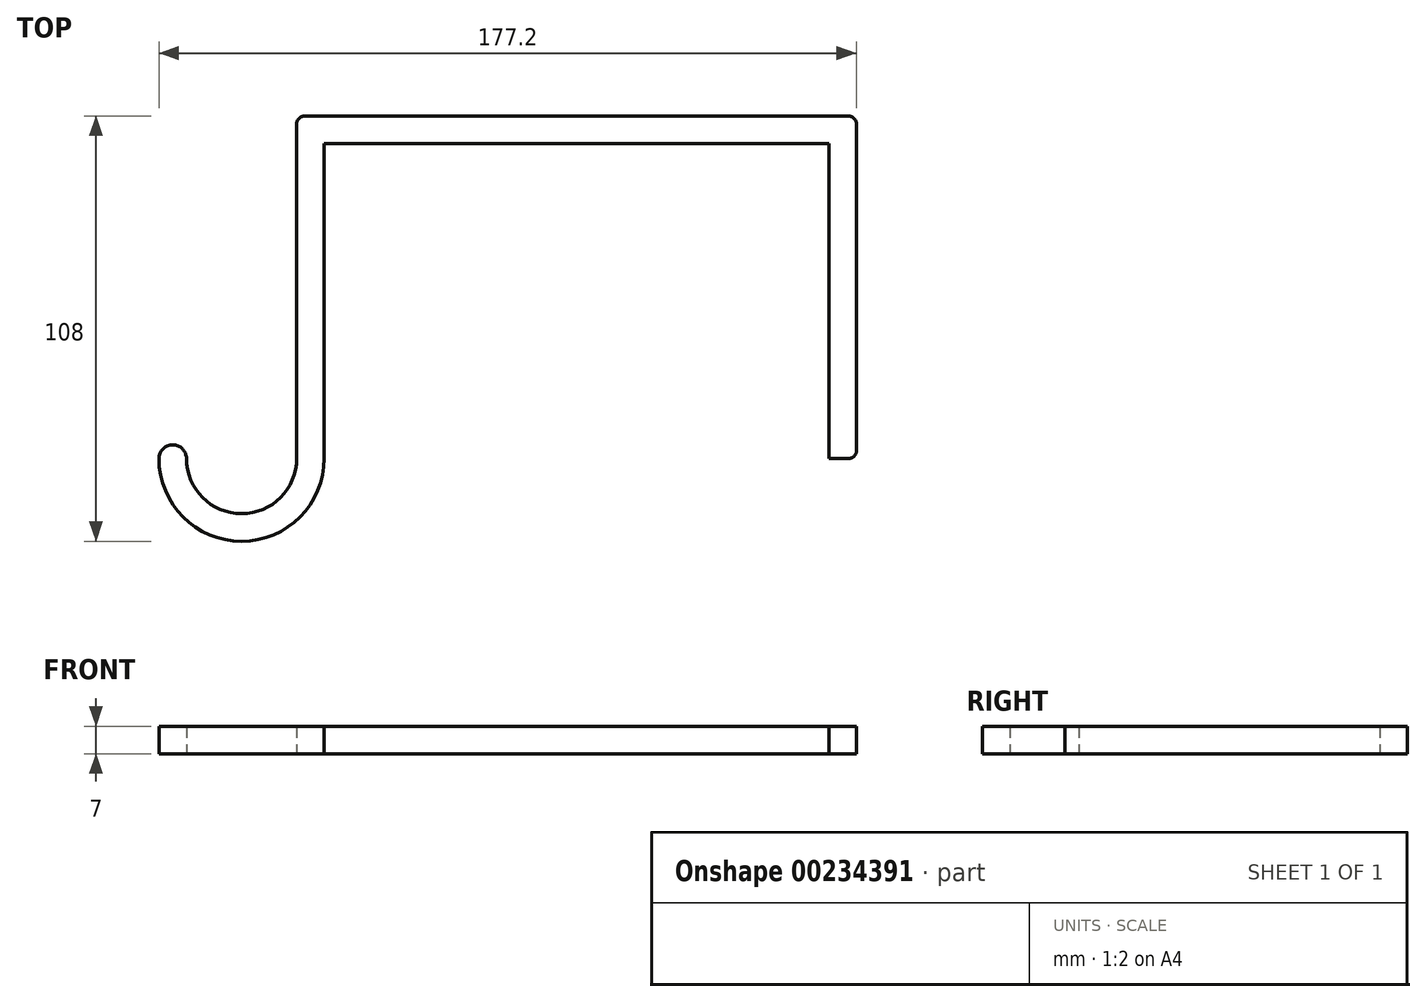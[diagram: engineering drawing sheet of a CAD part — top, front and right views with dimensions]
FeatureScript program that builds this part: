
annotation { "Feature Type Name" : "Feature", "Feature Type Description" : "" }
export const myFeature = defineFeature(function(context is Context, id is Id, definition is map)
    precondition{}
    {
        {
            assignVariable(context, id + "F0", {"name" : "D", "anyValue" : 7});
        }
        {
            var Q0;
            Q0=qCreatedBy(makeId("Top.planeOp"),FACE);
            var sketch = newSketch(context, id + "F1", { "sketchPlane" : qUnion([Q0])});
            skArc(sketch, "E0", {"start": v(-14, 0) * mm, "mid": v(0, -14) * mm, "end": v(14, 0) * mm});
            skLineSegment(sketch, "E1", {"start": v(14, 0) * mm, "end": v(14, 85) * mm});
            skLineSegment(sketch, "E2", {"start": v(16, 87) * mm, "end": v(154.2, 87) * mm});
            skLineSegment(sketch, "E3", {"start": v(156.2, 85) * mm, "end": v(156.2, 2) * mm});
            skLineSegment(sketch, "E4", {"start": v(154.2, 0) * mm, "end": v(149.2, 0) * mm});
            skLineSegment(sketch, "E5", {"start": v(149.2, 0) * mm, "end": v(149.2, 80) * mm});
            skLineSegment(sketch, "E6", {"start": v(149.2, 80) * mm, "end": v(21, 80) * mm});
            skLineSegment(sketch, "E7", {"start": v(21, 80) * mm, "end": v(21, 0) * mm});
            skArc(sketch, "E8", {"start": v(21, 0) * mm, "mid": v(0, -21) * mm, "end": v(-21, 0) * mm});
            skArc(sketch, "E9", {"start": v(-21, 0) * mm, "mid": v(-17.5, 3.5) * mm, "end": v(-14, 0) * mm});
            skPoint(sketch, "E10.visualSharp", {"position": v(14, 87) * mm});
            skArc(sketch, "E10.filletArc", {"start": v(16, 87) * mm, "mid": v(14.59, 86.41) * mm, "end": v(14, 85) * mm});
            skPoint(sketch, "E11.visualSharp", {"position": v(156.2, 87) * mm});
            skArc(sketch, "E11.filletArc", {"start": v(156.2, 85) * mm, "mid": v(155.61, 86.41) * mm, "end": v(154.2, 87) * mm});
            skPoint(sketch, "E12.visualSharp", {"position": v(156.2, 0) * mm});
            skArc(sketch, "E12.filletArc", {"start": v(154.2, 0) * mm, "mid": v(155.61, 0.59) * mm, "end": v(156.2, 2) * mm});
            skSolve(sketch);
        }
        {
            var Q0;
            Q0=makeQuery(id+"F1.imprint","IMPRINT",FACE,{"disambiguationData":[TD([[makeQuery(id+"F1.imprint","IMPRINT",EDGE,{"derivedFrom":sQuery(id+"F1.wireOp",EDGE,"E0")}),-1.0]])]});
            extrude(context, id + "F2", {"entities" : qUnion([Q0]), "depth" : getVariable(context, 'D') * mm});
        }
    });
